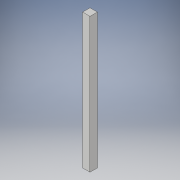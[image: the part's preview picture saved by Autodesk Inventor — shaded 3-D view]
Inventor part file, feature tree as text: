
AUTODESK INVENTOR PART (.ipt)
format: ipt  version: 2017 (Build 210142000, 142)  size: 99,328 bytes
history: native  units: in
note: dims shown in document units (in); Inventor stores cm internally (conversion verified against a paired STEP export)
features: extrude x2, sketch x2
ambient origin geometry x8: Origin, YZ Plane, XZ Plane, XY Plane, X Axis, Y Axis, Z Axis, Center Point
bodies: Solid1 (feature_tree)
feature tree (4):
  extrude  "Extrusion1"  Depth=3.0in
  extrude  "Extrusion2"  Depth=36.0in TaperAngle=0.0deg
  sketch  "Sketch1"  dims[d0=3.0in d1=3.0in]
  sketch  "Sketch2"  dims[d2=19.0in d3=0.0in d4=36.0in d5=0.0in]
